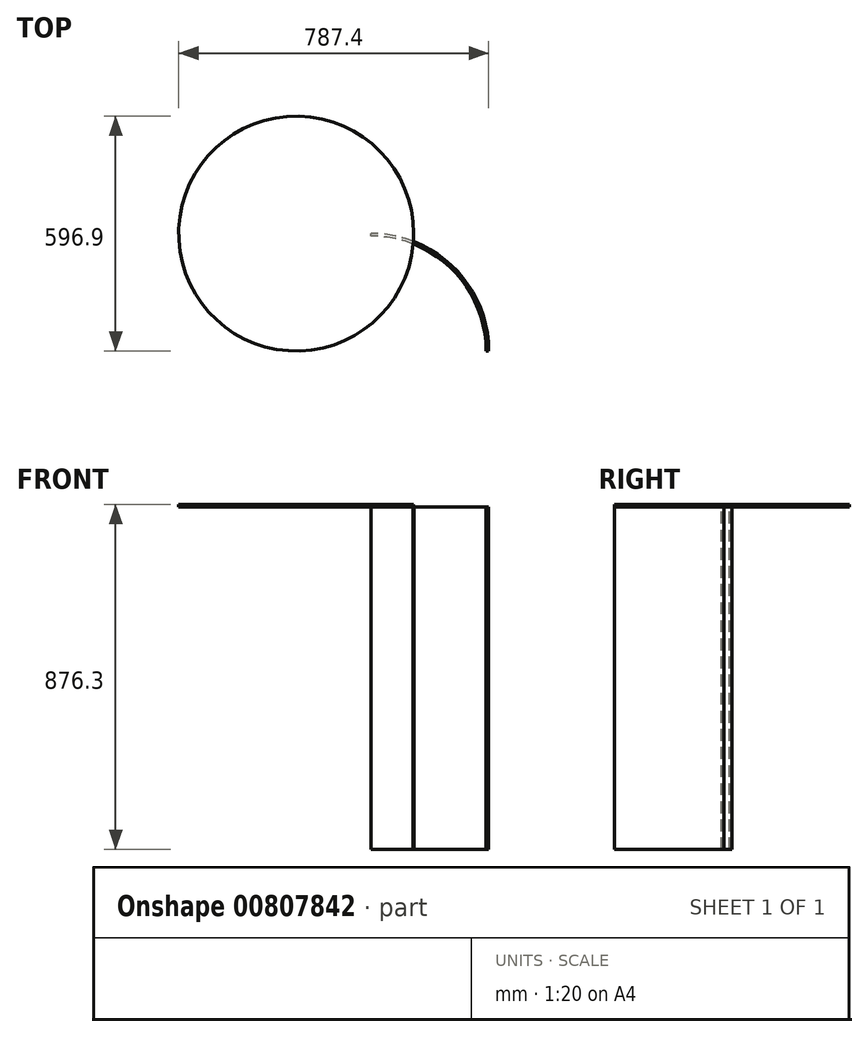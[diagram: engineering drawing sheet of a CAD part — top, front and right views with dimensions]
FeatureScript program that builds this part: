
annotation { "Feature Type Name" : "Feature", "Feature Type Description" : "" }
export const myFeature = defineFeature(function(context is Context, id is Id, definition is map)
    precondition{}
    {
        {
            var Q0;
            Q0=qCreatedBy(makeId("Top.planeOp"),FACE);
            var sketch = newSketch(context, id + "F0", { "sketchPlane" : qUnion([Q0])});
            skCircle(sketch, "E0", {"center": v(0, 0) * mm, "radius": 298.45 * mm});
            skSolve(sketch);
        }
        {
            var Q0;
            Q0=makeQuery(id+"F0.imprint","IMPRINT",FACE,{"disambiguationData":[TD([[makeQuery(id+"F0.imprint","IMPRINT",EDGE,{"derivedFrom":sQuery(id+"F0.wireOp",EDGE,"E0")}),1.0]])]});
            extrude(context, id + "F1", {"entities" : qUnion([Q0]), "depth" : 6.35 * mm, "offsetDistance" : 25.4 * mm});
        }
        {
            var Q0;
            Q0=makeQuery(id+"F1.opExtrude","CAP_FACE",FACE,{"disambiguationData":[OSD([sQuery(id+"F0.wireOp",EDGE,"E0")])],"isStart":true});
            var sketch = newSketch(context, id + "F2", { "sketchPlane" : qUnion([Q0])});
            skCircle(sketch, "E1", {"center": v(0, 0) * mm, "radius": 190.5 * mm});
            skCircle(sketch, "E2", {"center": v(0, 0) * mm, "radius": 300.08 * mm});
            skLineSegment(sketch, "E3", {"start": v(0, 0) * mm, "end": v(298.45, 0) * mm});
            skLineSegment(sketch, "E4", {"start": v(190.5, 0) * mm, "end": v(488.95, 0) * mm});
            skLineSegment(sketch, "E5", {"start": v(488.95, 0) * mm, "end": v(488.95, 298.45) * mm});
            skArc(sketch, "E6", {"start": v(190.5, 0) * mm, "mid": v(401.54, 87.41) * mm, "end": v(488.95, 298.45) * mm});
            skArc(sketch, "E7.0", {"start": v(190.5, 6.35) * mm, "mid": v(397.05, 91.9) * mm, "end": v(482.6, 298.45) * mm});
            skCircle(sketch, "E8.0", {"center": v(0, 0) * mm, "radius": 292.1 * mm});
            skLineSegment(sketch, "E9", {"start": v(482.6, 298.45) * mm, "end": v(488.95, 298.45) * mm});
            skLineSegment(sketch, "E10", {"start": v(190.5, 6.35) * mm, "end": v(190.5, 0) * mm});
            skSolve(sketch);
        }
        {
            var Q0;
            {var subQ0=sQuery(id+"F2.wireOp",EDGE,"E10");Q0=makeQuery(id+"F2.imprint","IMPRINT",FACE,{"disambiguationData":[TD([[makeQuery(id+"F2.imprint","IMPRINT",EDGE,{"derivedFrom":subQ0}),1.0]])]});}
            var Q1;
            {var subQ0=sQuery(id+"F2.wireOp",EDGE,"E8.0");var subQ1=sQuery(id+"F2.wireOp",EDGE,"E6");var subQ2=makeQuery(id+"F2.imprint","INTERSECT",VERTEX,{"derivedFrom":[subQ1,subQ0]});Q1=makeQuery(id+"F2.imprint","IMPRINT",FACE,{"disambiguationData":[TD([[makeQuery(id+"F2.imprint","IMPRINT",EDGE,{"disambiguationData":[TD([[subQ2,-1.0]])],"derivedFrom":subQ1}),1.0]])]});}
            var Q2;
            {var subQ5=sQuery(id+"F2.wireOp",EDGE,"E9");Q2=makeQuery(id+"F2.imprint","IMPRINT",FACE,{"disambiguationData":[TD([[makeQuery(id+"F2.imprint","IMPRINT",EDGE,{"derivedFrom":subQ5}),-1.0]])]});}
            extrude(context, id + "F3", {"entities" : qUnion([Q0, Q1, Q2]), "operationType" : NewBodyOperationType.ADD, "depth" : 869.95 * mm, "offsetDistance" : 25.4 * mm});
        }
    });
